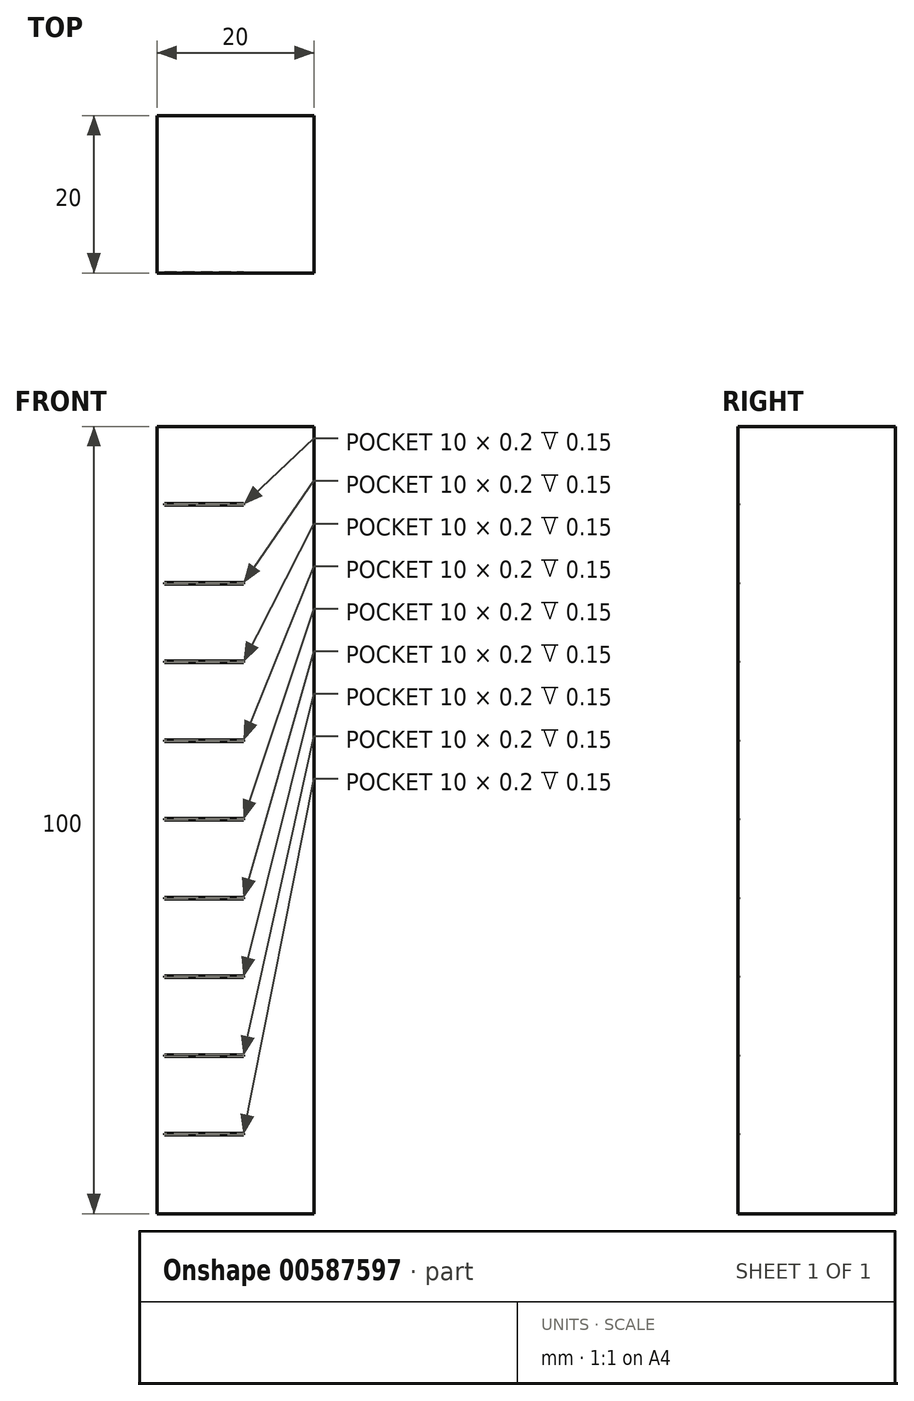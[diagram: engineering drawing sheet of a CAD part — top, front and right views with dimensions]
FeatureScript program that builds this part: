
annotation { "Feature Type Name" : "Feature", "Feature Type Description" : "" }
export const myFeature = defineFeature(function(context is Context, id is Id, definition is map)
    precondition{}
    {
        {
            var Q0;
            Q0=qCreatedBy(makeId("Top.planeOp"),FACE);
            var sketch = newSketch(context, id + "F0", { "sketchPlane" : qUnion([Q0])});
            skLineSegment(sketch, "E0.bottom", {"start": v(10, -10) * mm, "end": v(-10, -10) * mm});
            skLineSegment(sketch, "E0.top", {"start": v(10, 10) * mm, "end": v(-10, 10) * mm});
            skLineSegment(sketch, "E0.left", {"start": v(10, -10) * mm, "end": v(10, 10) * mm});
            skLineSegment(sketch, "E0.right", {"start": v(-10, -10) * mm, "end": v(-10, 10) * mm});
            skPoint(sketch, "E0.middle", {"position": v(0, 0) * mm});
            skSolve(sketch);
        }
        {
            var Q0;
            Q0 = qSketchRegion(id + "F0", true);
            extrude(context, id + "F1", {"entities" : qUnion([Q0]), "depth" : 100 * mm, "offsetDistance" : 25 * mm});
        }
        {
            var Q0;
            Q0=makeQuery(id+"F1.opExtrude","SWEPT_FACE",FACE,{"disambiguationData":[OSD([sQuery(id+"F0.wireOp",EDGE,"E0.bottom")])]});
            var sketch = newSketch(context, id + "F2", { "sketchPlane" : qUnion([Q0])});
            skLineSegment(sketch, "E1.bottom", {"start": v(-9, 10.2) * mm, "end": v(1, 10.2) * mm});
            skLineSegment(sketch, "E1.top", {"start": v(-9, 10) * mm, "end": v(1, 10) * mm});
            skLineSegment(sketch, "E1.left", {"start": v(-9, 10.2) * mm, "end": v(-9, 10) * mm});
            skLineSegment(sketch, "E1.right", {"start": v(1, 10.2) * mm, "end": v(1, 10) * mm});
            skLineSegment(sketch, "E2.0.1.0", {"start": v(-9, 20) * mm, "end": v(1, 20) * mm});
            skLineSegment(sketch, "E2.0.1.1", {"start": v(-9, 20.2) * mm, "end": v(1, 20.2) * mm});
            skLineSegment(sketch, "E2.0.1.2", {"start": v(1, 20.2) * mm, "end": v(1, 20) * mm});
            skLineSegment(sketch, "E2.0.1.3", {"start": v(-9, 20.2) * mm, "end": v(-9, 20) * mm});
            skLineSegment(sketch, "E2.0.2.0", {"start": v(-9, 30) * mm, "end": v(1, 30) * mm});
            skLineSegment(sketch, "E2.0.2.1", {"start": v(-9, 30.2) * mm, "end": v(1, 30.2) * mm});
            skLineSegment(sketch, "E2.0.2.2", {"start": v(1, 30.2) * mm, "end": v(1, 30) * mm});
            skLineSegment(sketch, "E2.0.2.3", {"start": v(-9, 30.2) * mm, "end": v(-9, 30) * mm});
            skLineSegment(sketch, "E2.0.3.0", {"start": v(-9, 40) * mm, "end": v(1, 40) * mm});
            skLineSegment(sketch, "E2.0.3.1", {"start": v(-9, 40.2) * mm, "end": v(1, 40.2) * mm});
            skLineSegment(sketch, "E2.0.3.2", {"start": v(1, 40.2) * mm, "end": v(1, 40) * mm});
            skLineSegment(sketch, "E2.0.3.3", {"start": v(-9, 40.2) * mm, "end": v(-9, 40) * mm});
            skLineSegment(sketch, "E2.0.4.0", {"start": v(-9, 50) * mm, "end": v(1, 50) * mm});
            skLineSegment(sketch, "E2.0.4.1", {"start": v(-9, 50.2) * mm, "end": v(1, 50.2) * mm});
            skLineSegment(sketch, "E2.0.4.2", {"start": v(1, 50.2) * mm, "end": v(1, 50) * mm});
            skLineSegment(sketch, "E2.0.4.3", {"start": v(-9, 50.2) * mm, "end": v(-9, 50) * mm});
            skLineSegment(sketch, "E2.0.5.0", {"start": v(-9, 60) * mm, "end": v(1, 60) * mm});
            skLineSegment(sketch, "E2.0.5.1", {"start": v(-9, 60.2) * mm, "end": v(1, 60.2) * mm});
            skLineSegment(sketch, "E2.0.5.2", {"start": v(1, 60.2) * mm, "end": v(1, 60) * mm});
            skLineSegment(sketch, "E2.0.5.3", {"start": v(-9, 60.2) * mm, "end": v(-9, 60) * mm});
            skLineSegment(sketch, "E2.0.6.0", {"start": v(-9, 70) * mm, "end": v(1, 70) * mm});
            skLineSegment(sketch, "E2.0.6.1", {"start": v(-9, 70.2) * mm, "end": v(1, 70.2) * mm});
            skLineSegment(sketch, "E2.0.6.2", {"start": v(1, 70.2) * mm, "end": v(1, 70) * mm});
            skLineSegment(sketch, "E2.0.6.3", {"start": v(-9, 70.2) * mm, "end": v(-9, 70) * mm});
            skLineSegment(sketch, "E2.0.7.0", {"start": v(-9, 80) * mm, "end": v(1, 80) * mm});
            skLineSegment(sketch, "E2.0.7.1", {"start": v(-9, 80.2) * mm, "end": v(1, 80.2) * mm});
            skLineSegment(sketch, "E2.0.7.2", {"start": v(1, 80.2) * mm, "end": v(1, 80) * mm});
            skLineSegment(sketch, "E2.0.7.3", {"start": v(-9, 80.2) * mm, "end": v(-9, 80) * mm});
            skLineSegment(sketch, "E2.0.8.0", {"start": v(-9, 90) * mm, "end": v(1, 90) * mm});
            skLineSegment(sketch, "E2.0.8.1", {"start": v(-9, 90.2) * mm, "end": v(1, 90.2) * mm});
            skLineSegment(sketch, "E2.0.8.2", {"start": v(1, 90.2) * mm, "end": v(1, 90) * mm});
            skLineSegment(sketch, "E2.0.8.3", {"start": v(-9, 90.2) * mm, "end": v(-9, 90) * mm});
            skLineSegment(sketch, "E2.0.9.0", {"start": v(-9, 100) * mm, "end": v(1, 100) * mm});
            skLineSegment(sketch, "E2.0.9.1", {"start": v(-9, 100.2) * mm, "end": v(1, 100.2) * mm});
            skLineSegment(sketch, "E2.0.9.2", {"start": v(1, 100.2) * mm, "end": v(1, 100) * mm});
            skLineSegment(sketch, "E2.0.9.3", {"start": v(-9, 100.2) * mm, "end": v(-9, 100) * mm});
            skLineSegment(sketch, "E2.direction1", {"start": v(-9, 10) * mm, "end": v(6.4, 10) * mm, "construction": true});
            skLineSegment(sketch, "E2.direction2", {"start": v(-9, 10) * mm, "end": v(-9, 20) * mm, "construction": true});
            skSolve(sketch);
        }
        {
            var Q0;
            Q0 = qSketchRegion(id + "F2", true);
            extrude(context, id + "F3", {"entities" : qUnion([Q0]), "operationType" : NewBodyOperationType.REMOVE, "oppositeDirection" : true, "depth" : .15 * mm, "offsetDistance" : 25 * mm});
        }
    });
